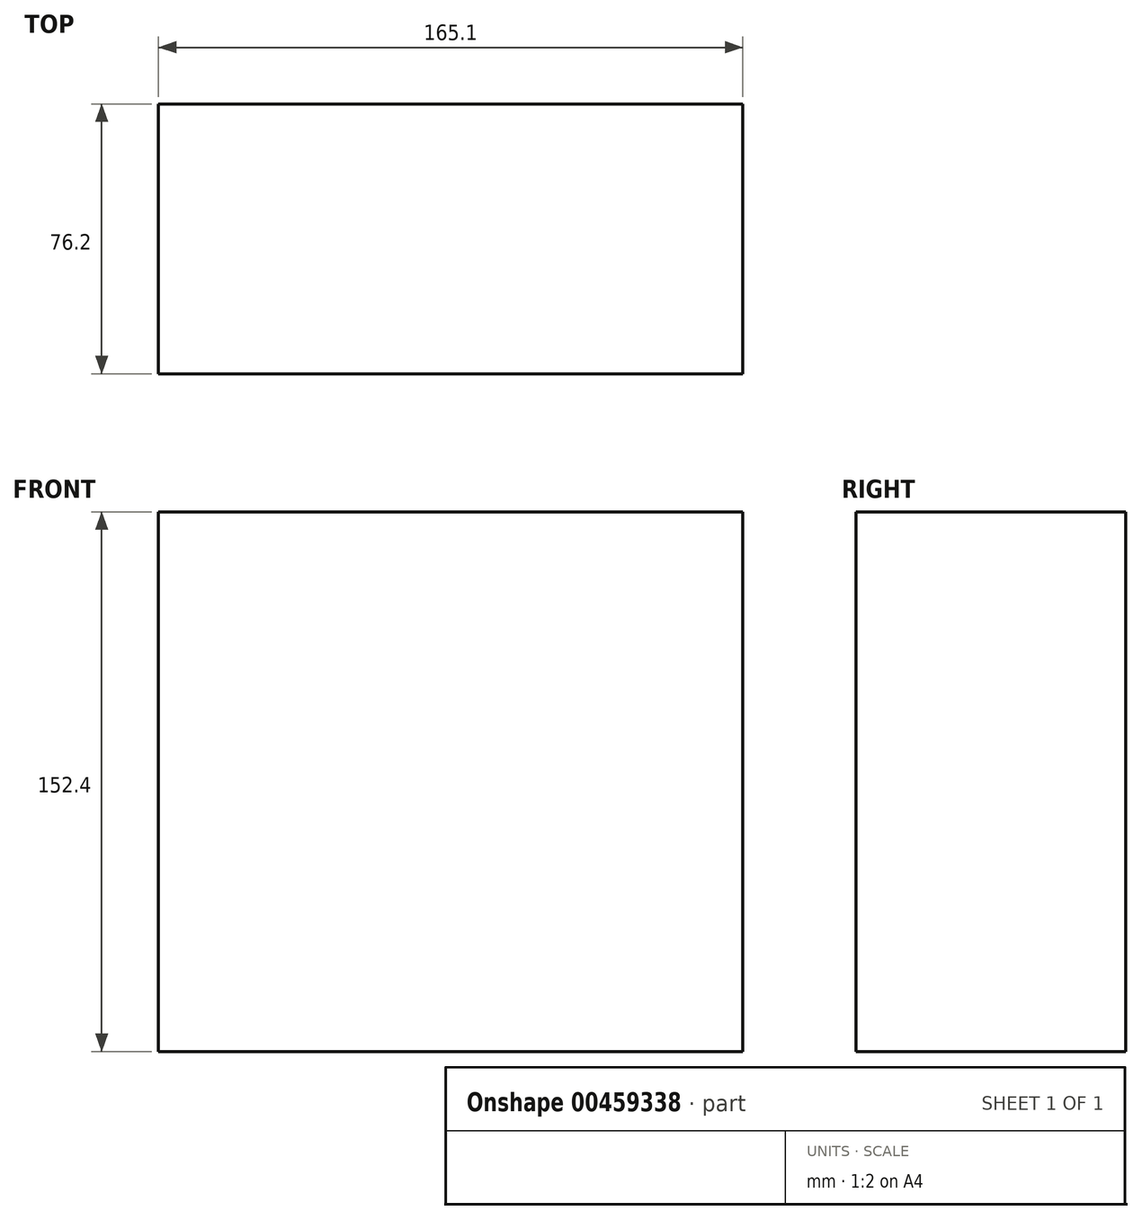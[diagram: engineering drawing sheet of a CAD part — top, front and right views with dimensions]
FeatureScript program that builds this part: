
annotation { "Feature Type Name" : "Feature", "Feature Type Description" : "" }
export const myFeature = defineFeature(function(context is Context, id is Id, definition is map)
    precondition{}
    {
        {
            var Q0;
            Q0=qCreatedBy(makeId("Top.planeOp"),FACE);
            var sketch = newSketch(context, id + "F0", { "sketchPlane" : qUnion([Q0])});
            skLineSegment(sketch, "E0.bottom", {"start": v(-114.3, 76.2) * mm, "end": v(114.3, 76.2) * mm});
            skLineSegment(sketch, "E0.top", {"start": v(-114.3, -76.2) * mm, "end": v(114.3, -76.2) * mm});
            skLineSegment(sketch, "E0.left", {"start": v(-114.3, 76.2) * mm, "end": v(-114.3, -76.2) * mm});
            skLineSegment(sketch, "E0.right", {"start": v(114.3, 76.2) * mm, "end": v(114.3, -76.2) * mm});
            skPoint(sketch, "E0.middle", {"position": v(0, 0) * mm});
            skLineSegment(sketch, "E1.bottom", {"start": v(114.3, 76.2) * mm, "end": v(-50.8, 76.2) * mm});
            skLineSegment(sketch, "E1.top", {"start": v(114.3, 0) * mm, "end": v(-50.8, 0) * mm});
            skLineSegment(sketch, "E1.left", {"start": v(114.3, 76.2) * mm, "end": v(114.3, 0) * mm});
            skLineSegment(sketch, "E1.right", {"start": v(-50.8, 76.2) * mm, "end": v(-50.8, 0) * mm});
            skSolve(sketch);
        }
        {
            var Q0;
            Q0=makeQuery(id+"F0.imprint","IMPRINT",FACE,{"disambiguationData":[TD([[makeQuery(id+"F0.imprint","IMPRINT",EDGE,{"derivedFrom":sQuery(id+"F0.wireOp",EDGE,"E0.bottom")}),-1.0]])]});
            extrude(context, id + "F1", {"entities" : qUnion([Q0]), "endBound" : BoundingType.SYMMETRIC, "depth" : 152.4 * mm});
        }
        {
            var Q0;
            Q0=makeQuery(id+"F1.opExtrude","SWEPT_FACE",FACE,{"disambiguationData":[OSD([sQuery(id+"F0.wireOp",EDGE,"E1.top")])]});
            var sketch = newSketch(context, id + "F2", { "sketchPlane" : qUnion([Q0])});
            skLineSegment(sketch, "E2.bottom", {"start": v(-114.3, 76.2) * mm, "end": v(-12.7, 76.2) * mm});
            skLineSegment(sketch, "E2.top", {"start": v(-114.3, 25.4) * mm, "end": v(-12.7, 25.4) * mm});
            skLineSegment(sketch, "E2.left", {"start": v(-114.3, 76.2) * mm, "end": v(-114.3, 25.4) * mm});
            skLineSegment(sketch, "E2.right", {"start": v(-12.7, 76.2) * mm, "end": v(-12.7, 25.4) * mm});
            skSolve(sketch);
        }
        {
            var Q0;
            Q0=makeQuery(id+"F2.imprint","IMPRINT",FACE,{"disambiguationData":[TD([[makeQuery(id+"F2.imprint","IMPRINT",EDGE,{"derivedFrom":sQuery(id+"F2.wireOp",EDGE,"E2.bottom")}),-1.0]])]});
            extrude(context, id + "F3", {"entities" : qUnion([Q0]), "operationType" : NewBodyOperationType.REMOVE, "endBound" : BoundingType.THROUGH_ALL, "oppositeDirection" : true, "depth" : 25.4 * mm});
        }
    });
